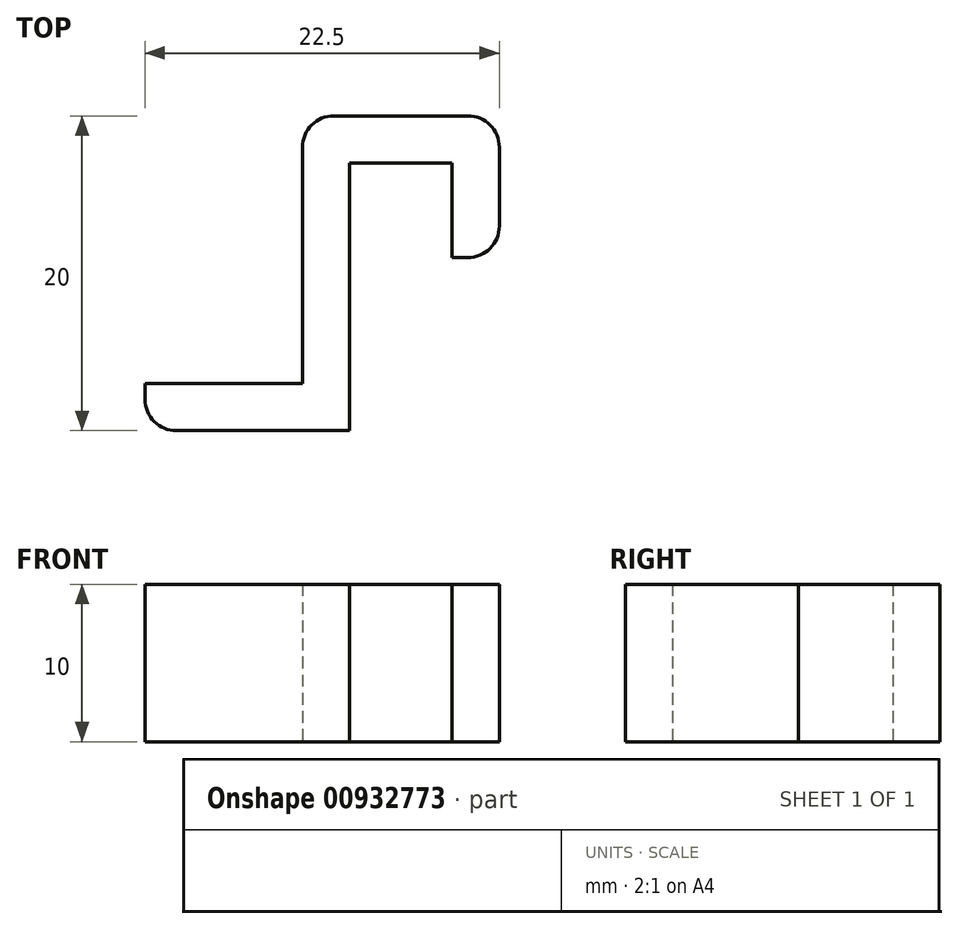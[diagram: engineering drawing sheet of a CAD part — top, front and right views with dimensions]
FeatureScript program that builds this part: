
annotation { "Feature Type Name" : "Feature", "Feature Type Description" : "" }
export const myFeature = defineFeature(function(context is Context, id is Id, definition is map)
    precondition{}
    {
        {
            var Q0;
            Q0=qCreatedBy(makeId("Top.planeOp"),FACE);
            var sketch = newSketch(context, id + "F0", { "sketchPlane" : qUnion([Q0])});
            skLineSegment(sketch, "E0.bottom", {"start": v(3.25, -1.5) * mm, "end": v(-3.25, -1.5) * mm});
            skLineSegment(sketch, "E0.top", {"start": v(3.25, 1.5) * mm, "end": v(-3.25, 1.5) * mm});
            skLineSegment(sketch, "E0.left", {"start": v(3.25, -1.5) * mm, "end": v(3.25, 1.5) * mm});
            skLineSegment(sketch, "E0.right", {"start": v(-3.25, -1.5) * mm, "end": v(-3.25, 1.5) * mm});
            skPoint(sketch, "E0.middle", {"position": v(0, 0) * mm});
            skLineSegment(sketch, "E1.bottom", {"start": v(3.25, 1.5) * mm, "end": v(6.25, 1.5) * mm});
            skLineSegment(sketch, "E1.top", {"start": v(3.25, -7.5) * mm, "end": v(6.25, -7.5) * mm});
            skLineSegment(sketch, "E1.left", {"start": v(3.25, 1.5) * mm, "end": v(3.25, -7.5) * mm});
            skLineSegment(sketch, "E1.right", {"start": v(6.25, 1.5) * mm, "end": v(6.25, -7.5) * mm});
            skLineSegment(sketch, "E2.bottom", {"start": v(-3.25, 1.5) * mm, "end": v(-6.25, 1.5) * mm});
            skLineSegment(sketch, "E2.top", {"start": v(-3.25, -18.5) * mm, "end": v(-6.25, -18.5) * mm});
            skLineSegment(sketch, "E2.left", {"start": v(-3.25, 1.5) * mm, "end": v(-3.25, -18.5) * mm});
            skLineSegment(sketch, "E2.right", {"start": v(-6.25, 1.5) * mm, "end": v(-6.25, -18.5) * mm});
            skLineSegment(sketch, "E3.bottom", {"start": v(-6.25, -18.5) * mm, "end": v(-16.25, -18.5) * mm});
            skLineSegment(sketch, "E3.top", {"start": v(-6.25, -15.5) * mm, "end": v(-16.25, -15.5) * mm});
            skLineSegment(sketch, "E3.left", {"start": v(-6.25, -18.5) * mm, "end": v(-6.25, -15.5) * mm});
            skLineSegment(sketch, "E3.right", {"start": v(-16.25, -18.5) * mm, "end": v(-16.25, -15.5) * mm});
            skSolve(sketch);
        }
        {
            var Q0;
            Q0=makeQuery(id+"F0.imprint","IMPRINT",FACE,{"disambiguationData":[TD([[makeQuery(id+"F0.imprint","IMPRINT",EDGE,{"derivedFrom":sQuery(id+"F0.wireOp",EDGE,"E3.bottom")}),-1.0]])]});
            var Q1;
            {var subQ3=sQuery(id+"F0.wireOp",EDGE,"E2.bottom");Q1=makeQuery(id+"F0.imprint","IMPRINT",FACE,{"disambiguationData":[TD([[makeQuery(id+"F0.imprint","IMPRINT",EDGE,{"derivedFrom":subQ3}),1.0]])]});}
            var Q2;
            {var subQ0=sQuery(id+"F0.wireOp",EDGE,"E0.bottom");Q2=makeQuery(id+"F0.imprint","IMPRINT",FACE,{"disambiguationData":[TD([[makeQuery(id+"F0.imprint","IMPRINT",EDGE,{"derivedFrom":subQ0}),-1.0]])]});}
            var Q3;
            {var subQ3=sQuery(id+"F0.wireOp",EDGE,"E1.bottom");Q3=makeQuery(id+"F0.imprint","IMPRINT",FACE,{"disambiguationData":[TD([[makeQuery(id+"F0.imprint","IMPRINT",EDGE,{"derivedFrom":subQ3}),-1.0]])]});}
            extrude(context, id + "F1", {"entities" : qUnion([Q0, Q1, Q2, Q3]), "depth" : 10 * mm, "offsetDistance" : 25 * mm});
        }
        {
            var Q0;
            Q0=makeQuery(id+"F1.opExtrude","SWEPT_EDGE",EDGE,{"disambiguationData":[OSD([sQuery(id+"F0.wireOp",EDGE,"E2.bottom"),sQuery(id+"F0.wireOp",EDGE,"E2.right")])]});
            var Q1;
            Q1=makeQuery(id+"F1.opExtrude","SWEPT_EDGE",EDGE,{"disambiguationData":[OSD([sQuery(id+"F0.wireOp",EDGE,"E1.bottom"),sQuery(id+"F0.wireOp",EDGE,"E1.right")])]});
            var Q2;
            Q2=makeQuery(id+"F1.opExtrude","SWEPT_EDGE",EDGE,{"disambiguationData":[OSD([sQuery(id+"F0.wireOp",EDGE,"E1.top"),sQuery(id+"F0.wireOp",EDGE,"E1.right")])]});
            var Q3;
            Q3=makeQuery(id+"F1.opExtrude","SWEPT_EDGE",EDGE,{"disambiguationData":[OSD([sQuery(id+"F0.wireOp",EDGE,"E3.bottom"),sQuery(id+"F0.wireOp",EDGE,"E3.right")])]});
            fillet(context, id + "F2", {"entities" : qUnion([Q0, Q1, Q2, Q3]), "radius" : 2 * mm, "tangentPropagation" : true, "allowEdgeOverflow" : false});
        }
    });
